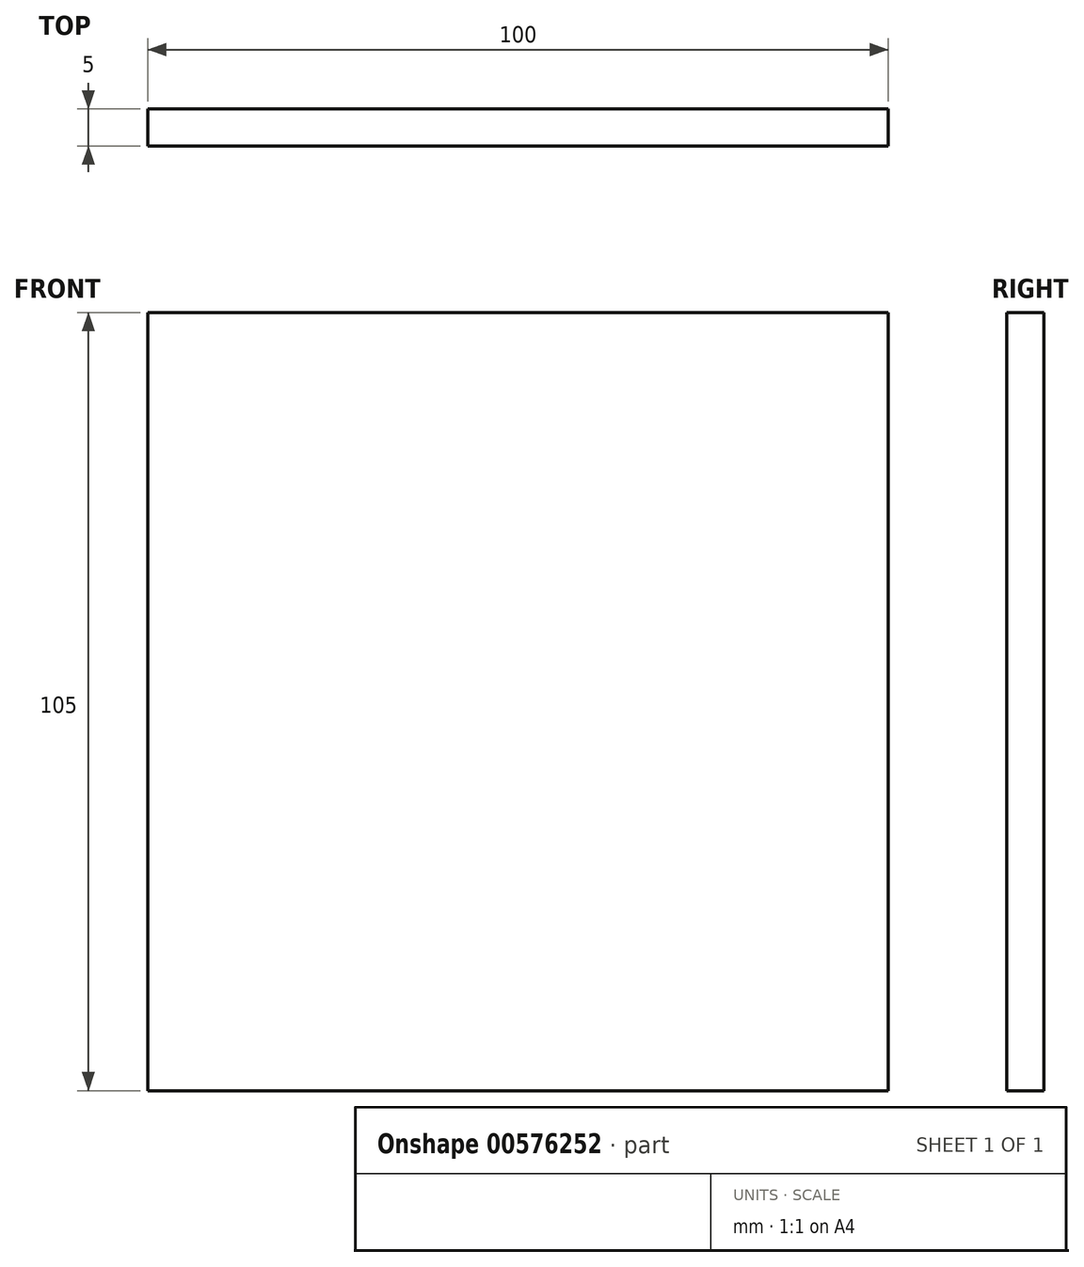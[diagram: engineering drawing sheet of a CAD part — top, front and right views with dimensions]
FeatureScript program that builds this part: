
annotation { "Feature Type Name" : "Feature", "Feature Type Description" : "" }
export const myFeature = defineFeature(function(context is Context, id is Id, definition is map)
    precondition{}
    {
        {
            var Q0;
            Q0=qCreatedBy(makeId("Front.planeOp"),FACE);
            var sketch = newSketch(context, id + "F0", { "sketchPlane" : qUnion([Q0])});
            skLineSegment(sketch, "E0.top", {"start": v(50, -50) * mm, "end": v(-50, -50) * mm});
            skLineSegment(sketch, "E0.left", {"start": v(50, 50) * mm, "end": v(50, -50) * mm});
            skLineSegment(sketch, "E0.right", {"start": v(-50, 50) * mm, "end": v(-50, -50) * mm});
            skPoint(sketch, "E0.middle", {"position": v(0, 0) * mm});
            skLineSegment(sketch, "E1", {"start": v(50, 50) * mm, "end": v(50, 55) * mm});
            skLineSegment(sketch, "E2", {"start": v(50, 55) * mm, "end": v(-50, 55) * mm});
            skLineSegment(sketch, "E3", {"start": v(-50, 55) * mm, "end": v(-50, 50) * mm});
            skSolve(sketch);
        }
        {
            var Q0;
            Q0 = qSketchRegion(id + "F0", true);
            extrude(context, id + "F1", {"entities" : qUnion([Q0]), "depth" : 5 * mm, "offsetDistance" : 25 * mm});
        }
    });
